SOLIDWORKS PART (.sldprt)
format: sldprt  version: not decoded by parser v0  size: 114,688 bytes
history: native  units: mm
features: sketch x5, cut_extrude x4, material x1, extrude x1 (+12 scaffold rows collapsed)
feature tree (23):
  scaffold x12  (default folders/planes/origin — collapsed)
  material  "Material <not specified>"
  sketch  "Sketch1"  dims[D1=4.0mm]
  extrude  "Boss-Extrude1"  Depth=8.2mm
  sketch  "Sketch2"  dims[D3=13.0mm D1=11.7mm D2=15.0mm]
  cut_extrude  "Cut-Extrude1"  Depth=7.2mm
  sketch  "Sketch3"  dims[D1=10.7mm]
  cut_extrude  "Cut-Extrude2"  Depth=9.9mm
  sketch  "Sketch4"  dims[D1=8.65mm]
  cut_extrude  "Cut-Extrude3"  Depth=13.9mm
  sketch  "Sketch5"  dims[D1=6.0mm]
  cut_extrude  "Cut-Extrude4"  Depth=1.4mm
decode coverage: 10 of 10 modeling features carry decoded parameters
note: suppression state not decoded; provenance and decode notes live in map.json
